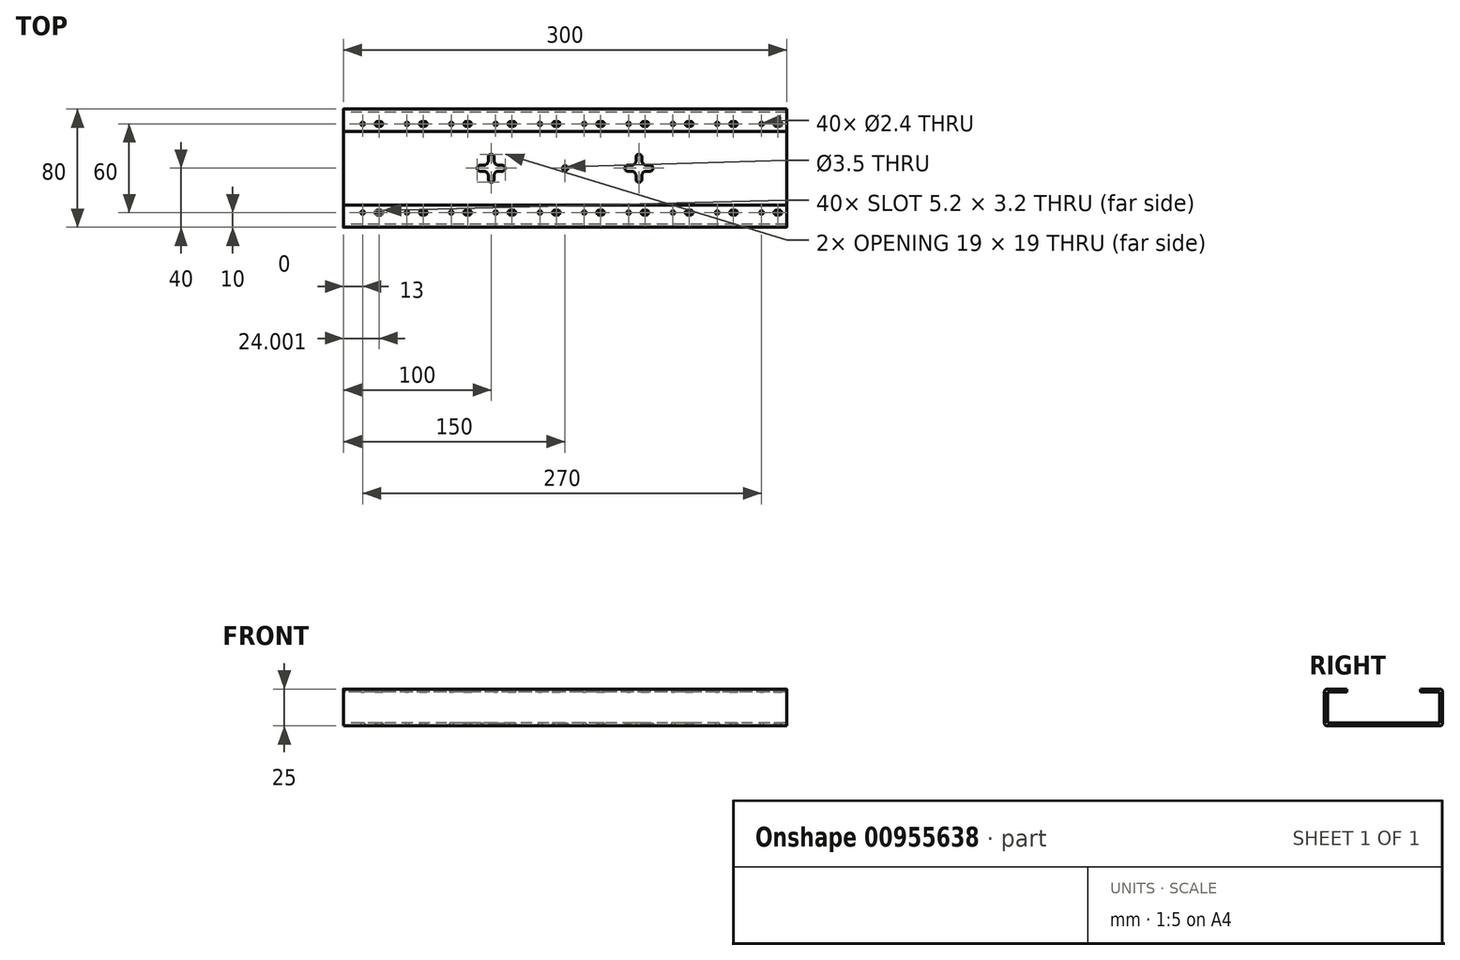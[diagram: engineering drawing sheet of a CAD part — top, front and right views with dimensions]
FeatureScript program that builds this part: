
annotation { "Feature Type Name" : "Feature", "Feature Type Description" : "" }
export const myFeature = defineFeature(function(context is Context, id is Id, definition is map)
    precondition{}
    {
        {
            var Q0;
            Q0=qCreatedBy(makeId("Right.planeOp"),FACE);
            var sketch = newSketch(context, id + "F0", { "sketchPlane" : qUnion([Q0])});
            skLineSegment(sketch, "E0", {"start": v(0, 0) * mm, "end": v(40, 0) * mm});
            skLineSegment(sketch, "E1", {"start": v(40, 0) * mm, "end": v(40, 25) * mm});
            skLineSegment(sketch, "E2", {"start": v(40, 25) * mm, "end": v(25, 25) * mm});
            skLineSegment(sketch, "E3", {"start": v(0, 0) * mm, "end": v(-40, 0) * mm});
            skLineSegment(sketch, "E4", {"start": v(-40, 0) * mm, "end": v(-40, 25) * mm});
            skLineSegment(sketch, "E5", {"start": v(-40, 25) * mm, "end": v(-25, 25) * mm});
            skLineSegment(sketch, "E6.0", {"start": v(38, 23) * mm, "end": v(25, 23) * mm});
            skLineSegment(sketch, "E6.1", {"start": v(38, 2) * mm, "end": v(38, 23) * mm});
            skLineSegment(sketch, "E6.2", {"start": v(-38, 23) * mm, "end": v(-25, 23) * mm});
            skLineSegment(sketch, "E6.3", {"start": v(-38, 2) * mm, "end": v(-38, 23) * mm});
            skLineSegment(sketch, "E6.4", {"start": v(0, 2) * mm, "end": v(-38, 2) * mm});
            skLineSegment(sketch, "E6.5", {"start": v(0, 2) * mm, "end": v(38, 2) * mm});
            skLineSegment(sketch, "E7", {"start": v(25, 25) * mm, "end": v(25, 23) * mm});
            skLineSegment(sketch, "E8", {"start": v(-25, 23) * mm, "end": v(-25, 25) * mm});
            skSolve(sketch);
        }
        {
            var Q0;
            Q0 = qSketchRegion(id + "F0", true);
            var Q1;
            Q1=sQuery(id+"F0.wireOp",EDGE,"E0");
            var Q2;
            Q2=sQuery(id+"F0.wireOp",EDGE,"E1");
            var Q3;
            Q3=sQuery(id+"F0.wireOp",EDGE,"E2");
            var Q4;
            Q4=sQuery(id+"F0.wireOp",EDGE,"E3");
            var Q5;
            Q5=sQuery(id+"F0.wireOp",EDGE,"E4");
            var Q6;
            Q6=sQuery(id+"F0.wireOp",EDGE,"E5");
            var Q7;
            Q7=sQuery(id+"F0.wireOp",EDGE,"E6.0");
            var Q8;
            Q8=sQuery(id+"F0.wireOp",EDGE,"E7");
            var Q9;
            Q9=sQuery(id+"F0.wireOp",EDGE,"E6.1");
            var Q10;
            Q10=sQuery(id+"F0.wireOp",EDGE,"E6.5");
            var Q11;
            Q11=sQuery(id+"F0.wireOp",EDGE,"E6.4");
            var Q12;
            Q12=sQuery(id+"F0.wireOp",EDGE,"E6.3");
            var Q13;
            Q13=sQuery(id+"F0.wireOp",EDGE,"E6.2");
            var Q14;
            Q14=sQuery(id+"F0.wireOp",EDGE,"E8");
            extrude(context, id + "F1", {"entities" : qUnion([Q0]), "surfaceEntities" : qUnion([Q1, Q2, Q3, Q4, Q5, Q6, Q7, Q8, Q9, Q10, Q11, Q12, Q13, Q14]), "endBound" : BoundingType.SYMMETRIC, "depth" : 300 * mm, "offsetDistance" : 25 * mm});
        }
        {
            var Q0;
            Q0=makeQuery(id+"F1.opExtrude","SWEPT_FACE",FACE,{"disambiguationData":[OSD([sQuery(id+"F0.wireOp",EDGE,"E0"),sQuery(id+"F0.wireOp",EDGE,"E3")])]});
            var sketch = newSketch(context, id + "F2", { "sketchPlane" : qUnion([Q0])});
            skCircle(sketch, "E9", {"center": v(133, 30) * mm, "radius": 1.2 * mm});
            skLineSegment(sketch, "E10", {"start": v(142.9, 31.6) * mm, "end": v(145, 31.6) * mm});
            skLineSegment(sketch, "E11", {"start": v(142.97, 28.4) * mm, "end": v(145.03, 28.4) * mm});
            skArc(sketch, "E12", {"start": v(142.9, 31.6) * mm, "mid": v(141.4, 29.93) * mm, "end": v(143.03, 28.4) * mm});
            skArc(sketch, "E13", {"start": v(145.03, 28.4) * mm, "mid": v(146.6, 30.02) * mm, "end": v(145, 31.6) * mm});
            skLineSegment(sketch, "E14.1.0.0", {"start": v(112.97, 28.4) * mm, "end": v(115.03, 28.4) * mm});
            skCircle(sketch, "E14.1.0.1", {"center": v(103, 30) * mm, "radius": 1.2 * mm});
            skArc(sketch, "E14.1.0.2", {"start": v(112.9, 31.6) * mm, "mid": v(111.4, 29.93) * mm, "end": v(113.03, 28.4) * mm});
            skArc(sketch, "E14.1.0.3", {"start": v(115.03, 28.4) * mm, "mid": v(116.6, 30.02) * mm, "end": v(115, 31.6) * mm});
            skLineSegment(sketch, "E14.1.0.4", {"start": v(112.9, 31.6) * mm, "end": v(115, 31.6) * mm});
            skLineSegment(sketch, "E14.2.0.0", {"start": v(82.97, 28.4) * mm, "end": v(85.03, 28.4) * mm});
            skCircle(sketch, "E14.2.0.1", {"center": v(73, 30) * mm, "radius": 1.2 * mm});
            skArc(sketch, "E14.2.0.2", {"start": v(82.9, 31.6) * mm, "mid": v(81.4, 29.93) * mm, "end": v(83.03, 28.4) * mm});
            skArc(sketch, "E14.2.0.3", {"start": v(85.03, 28.4) * mm, "mid": v(86.6, 30.02) * mm, "end": v(85, 31.6) * mm});
            skLineSegment(sketch, "E14.2.0.4", {"start": v(82.9, 31.6) * mm, "end": v(85, 31.6) * mm});
            skLineSegment(sketch, "E14.direction1", {"start": v(133, 30) * mm, "end": v(103, 30) * mm, "construction": true});
            skLineSegment(sketch, "E15.0.3.0", {"start": v(52.97, 28.4) * mm, "end": v(55.03, 28.4) * mm});
            skCircle(sketch, "E15.3.3.0", {"center": v(43, 30) * mm, "radius": 1.2 * mm});
            skArc(sketch, "E15.5.3.0", {"start": v(52.9, 31.6) * mm, "mid": v(51.4, 29.93) * mm, "end": v(53.03, 28.4) * mm});
            skArc(sketch, "E15.9.3.0", {"start": v(55.03, 28.4) * mm, "mid": v(56.6, 30.02) * mm, "end": v(55, 31.6) * mm});
            skLineSegment(sketch, "E15.13.3.0", {"start": v(52.9, 31.6) * mm, "end": v(55, 31.6) * mm});
            skLineSegment(sketch, "E15.0.4.0", {"start": v(22.97, 28.4) * mm, "end": v(25.03, 28.4) * mm});
            skCircle(sketch, "E15.3.4.0", {"center": v(13, 30) * mm, "radius": 1.2 * mm});
            skArc(sketch, "E15.5.4.0", {"start": v(22.9, 31.6) * mm, "mid": v(21.4, 29.93) * mm, "end": v(23.03, 28.4) * mm});
            skArc(sketch, "E15.9.4.0", {"start": v(25.03, 28.4) * mm, "mid": v(26.6, 30.02) * mm, "end": v(25, 31.6) * mm});
            skLineSegment(sketch, "E15.13.4.0", {"start": v(22.9, 31.6) * mm, "end": v(25, 31.6) * mm});
            skLineSegment(sketch, "E15.0.5.0", {"start": v(-7.03, 28.4) * mm, "end": v(-4.97, 28.4) * mm});
            skCircle(sketch, "E15.3.5.0", {"center": v(-17, 30) * mm, "radius": 1.2 * mm});
            skArc(sketch, "E15.5.5.0", {"start": v(-7.1, 31.6) * mm, "mid": v(-8.6, 29.93) * mm, "end": v(-6.97, 28.4) * mm});
            skArc(sketch, "E15.9.5.0", {"start": v(-4.97, 28.4) * mm, "mid": v(-3.4, 30.02) * mm, "end": v(-5, 31.6) * mm});
            skLineSegment(sketch, "E15.13.5.0", {"start": v(-7.1, 31.6) * mm, "end": v(-5, 31.6) * mm});
            skLineSegment(sketch, "E15.0.6.0", {"start": v(-37.03, 28.4) * mm, "end": v(-34.97, 28.4) * mm});
            skCircle(sketch, "E15.3.6.0", {"center": v(-47, 30) * mm, "radius": 1.2 * mm});
            skArc(sketch, "E15.5.6.0", {"start": v(-37.1, 31.6) * mm, "mid": v(-38.6, 29.93) * mm, "end": v(-36.97, 28.4) * mm});
            skArc(sketch, "E15.9.6.0", {"start": v(-34.97, 28.4) * mm, "mid": v(-33.4, 30.02) * mm, "end": v(-35, 31.6) * mm});
            skLineSegment(sketch, "E15.13.6.0", {"start": v(-37.1, 31.6) * mm, "end": v(-35, 31.6) * mm});
            skLineSegment(sketch, "E15.0.7.0", {"start": v(-67.03, 28.4) * mm, "end": v(-64.97, 28.4) * mm});
            skCircle(sketch, "E15.3.7.0", {"center": v(-77, 30) * mm, "radius": 1.2 * mm});
            skArc(sketch, "E15.5.7.0", {"start": v(-67.1, 31.6) * mm, "mid": v(-68.6, 29.93) * mm, "end": v(-66.97, 28.4) * mm});
            skArc(sketch, "E15.9.7.0", {"start": v(-64.97, 28.4) * mm, "mid": v(-63.4, 30.02) * mm, "end": v(-65, 31.6) * mm});
            skLineSegment(sketch, "E15.13.7.0", {"start": v(-67.1, 31.6) * mm, "end": v(-65, 31.6) * mm});
            skLineSegment(sketch, "E15.0.8.0", {"start": v(-97.03, 28.4) * mm, "end": v(-94.97, 28.4) * mm});
            skCircle(sketch, "E15.3.8.0", {"center": v(-107, 30) * mm, "radius": 1.2 * mm});
            skArc(sketch, "E15.5.8.0", {"start": v(-97.1, 31.6) * mm, "mid": v(-98.6, 29.93) * mm, "end": v(-96.97, 28.4) * mm});
            skArc(sketch, "E15.9.8.0", {"start": v(-94.97, 28.4) * mm, "mid": v(-93.4, 30.02) * mm, "end": v(-95, 31.6) * mm});
            skLineSegment(sketch, "E15.13.8.0", {"start": v(-97.1, 31.6) * mm, "end": v(-95, 31.6) * mm});
            skLineSegment(sketch, "E15.0.9.0", {"start": v(-127.03, 28.4) * mm, "end": v(-124.97, 28.4) * mm});
            skCircle(sketch, "E15.3.9.0", {"center": v(-137, 30) * mm, "radius": 1.2 * mm});
            skArc(sketch, "E15.5.9.0", {"start": v(-127.1, 31.6) * mm, "mid": v(-128.6, 29.93) * mm, "end": v(-126.97, 28.4) * mm});
            skArc(sketch, "E15.9.9.0", {"start": v(-124.97, 28.4) * mm, "mid": v(-123.4, 30.02) * mm, "end": v(-125, 31.6) * mm});
            skLineSegment(sketch, "E15.13.9.0", {"start": v(-127.1, 31.6) * mm, "end": v(-125, 31.6) * mm});
            skLineSegment(sketch, "E16.MirrorCS", {"start": v(-127.1, -31.6) * mm, "end": v(-125, -31.6) * mm});
            skLineSegment(sketch, "E17.MirrorCS", {"start": v(-127.03, -28.4) * mm, "end": v(-124.97, -28.4) * mm});
            skArc(sketch, "E18.MirrorCS", {"start": v(-127.1, -31.6) * mm, "mid": v(-128.6, -29.93) * mm, "end": v(-126.97, -28.4) * mm});
            skArc(sketch, "E19.MirrorCS", {"start": v(-124.97, -28.4) * mm, "mid": v(-123.4, -30.02) * mm, "end": v(-125, -31.6) * mm});
            skCircle(sketch, "E20.MirrorC", {"center": v(-137, -30) * mm, "radius": 1.2 * mm});
            skLineSegment(sketch, "E21.MirrorCS", {"start": v(-97.03, -28.4) * mm, "end": v(-94.97, -28.4) * mm});
            skLineSegment(sketch, "E22.MirrorCS", {"start": v(-97.1, -31.6) * mm, "end": v(-95, -31.6) * mm});
            skArc(sketch, "E23.MirrorCS", {"start": v(-94.97, -28.4) * mm, "mid": v(-93.4, -30.02) * mm, "end": v(-95, -31.6) * mm});
            skArc(sketch, "E24.MirrorCS", {"start": v(-97.1, -31.6) * mm, "mid": v(-98.6, -29.93) * mm, "end": v(-96.97, -28.4) * mm});
            skCircle(sketch, "E25.MirrorC", {"center": v(-107, -30) * mm, "radius": 1.2 * mm});
            skLineSegment(sketch, "E26.MirrorCS", {"start": v(-67.1, -31.6) * mm, "end": v(-65, -31.6) * mm});
            skLineSegment(sketch, "E27.MirrorCS", {"start": v(-67.03, -28.4) * mm, "end": v(-64.97, -28.4) * mm});
            skArc(sketch, "E28.MirrorCS", {"start": v(-67.1, -31.6) * mm, "mid": v(-68.6, -29.93) * mm, "end": v(-66.97, -28.4) * mm});
            skArc(sketch, "E29.MirrorCS", {"start": v(-64.97, -28.4) * mm, "mid": v(-63.4, -30.02) * mm, "end": v(-65, -31.6) * mm});
            skCircle(sketch, "E30.MirrorC", {"center": v(-77, -30) * mm, "radius": 1.2 * mm});
            skLineSegment(sketch, "E31.MirrorCS", {"start": v(-37.1, -31.6) * mm, "end": v(-35, -31.6) * mm});
            skArc(sketch, "E32.MirrorCS", {"start": v(-37.1, -31.6) * mm, "mid": v(-38.6, -29.93) * mm, "end": v(-36.97, -28.4) * mm});
            skArc(sketch, "E33.MirrorCS", {"start": v(-34.97, -28.4) * mm, "mid": v(-33.4, -30.02) * mm, "end": v(-35, -31.6) * mm});
            skLineSegment(sketch, "E34.MirrorCS", {"start": v(-37.03, -28.4) * mm, "end": v(-34.97, -28.4) * mm});
            skCircle(sketch, "E35.MirrorC", {"center": v(-47, -30) * mm, "radius": 1.2 * mm});
            skLineSegment(sketch, "E36.MirrorCS", {"start": v(-7.03, -28.4) * mm, "end": v(-4.97, -28.4) * mm});
            skArc(sketch, "E37.MirrorCS", {"start": v(-7.1, -31.6) * mm, "mid": v(-8.6, -29.93) * mm, "end": v(-6.97, -28.4) * mm});
            skArc(sketch, "E38.MirrorCS", {"start": v(-4.97, -28.4) * mm, "mid": v(-3.4, -30.02) * mm, "end": v(-5, -31.6) * mm});
            skLineSegment(sketch, "E39.MirrorCS", {"start": v(-7.1, -31.6) * mm, "end": v(-5, -31.6) * mm});
            skCircle(sketch, "E40.MirrorC", {"center": v(-17, -30) * mm, "radius": 1.2 * mm});
            skLineSegment(sketch, "E41.MirrorCS", {"start": v(22.9, -31.6) * mm, "end": v(25, -31.6) * mm});
            skArc(sketch, "E42.MirrorCS", {"start": v(25.03, -28.4) * mm, "mid": v(26.6, -30.02) * mm, "end": v(25, -31.6) * mm});
            skLineSegment(sketch, "E43.MirrorCS", {"start": v(22.97, -28.4) * mm, "end": v(25.03, -28.4) * mm});
            skArc(sketch, "E44.MirrorCS", {"start": v(22.9, -31.6) * mm, "mid": v(21.4, -29.93) * mm, "end": v(23.03, -28.4) * mm});
            skCircle(sketch, "E45.MirrorC", {"center": v(13, -30) * mm, "radius": 1.2 * mm});
            skLineSegment(sketch, "E46.MirrorCS", {"start": v(52.9, -31.6) * mm, "end": v(55, -31.6) * mm});
            skArc(sketch, "E47.MirrorCS", {"start": v(52.9, -31.6) * mm, "mid": v(51.4, -29.93) * mm, "end": v(53.03, -28.4) * mm});
            skArc(sketch, "E48.MirrorCS", {"start": v(55.03, -28.4) * mm, "mid": v(56.6, -30.02) * mm, "end": v(55, -31.6) * mm});
            skLineSegment(sketch, "E49.MirrorCS", {"start": v(52.97, -28.4) * mm, "end": v(55.03, -28.4) * mm});
            skCircle(sketch, "E50.MirrorC", {"center": v(43, -30) * mm, "radius": 1.2 * mm});
            skCircle(sketch, "E51.MirrorC", {"center": v(73, -30) * mm, "radius": 1.2 * mm});
            skLineSegment(sketch, "E52.MirrorCS", {"start": v(82.97, -28.4) * mm, "end": v(85.03, -28.4) * mm});
            skArc(sketch, "E53.MirrorCS", {"start": v(85.03, -28.4) * mm, "mid": v(86.6, -30.02) * mm, "end": v(85, -31.6) * mm});
            skLineSegment(sketch, "E54.MirrorCS", {"start": v(82.9, -31.6) * mm, "end": v(85, -31.6) * mm});
            skArc(sketch, "E55.MirrorCS", {"start": v(82.9, -31.6) * mm, "mid": v(81.4, -29.93) * mm, "end": v(83.03, -28.4) * mm});
            skLineSegment(sketch, "E56.MirrorCS", {"start": v(112.9, -31.6) * mm, "end": v(115, -31.6) * mm});
            skLineSegment(sketch, "E57.MirrorCS", {"start": v(142.9, -31.6) * mm, "end": v(145, -31.6) * mm});
            skArc(sketch, "E58.MirrorCS", {"start": v(142.9, -31.6) * mm, "mid": v(141.4, -29.93) * mm, "end": v(143.03, -28.4) * mm});
            skLineSegment(sketch, "E59.MirrorCS", {"start": v(112.97, -28.4) * mm, "end": v(115.03, -28.4) * mm});
            skLineSegment(sketch, "E60.MirrorCS", {"start": v(142.97, -28.4) * mm, "end": v(145.03, -28.4) * mm});
            skCircle(sketch, "E61.MirrorC", {"center": v(133, -30) * mm, "radius": 1.2 * mm});
            skArc(sketch, "E62.MirrorCS", {"start": v(145.03, -28.4) * mm, "mid": v(146.6, -30.02) * mm, "end": v(145, -31.6) * mm});
            skArc(sketch, "E63.MirrorCS", {"start": v(112.9, -31.6) * mm, "mid": v(111.4, -29.93) * mm, "end": v(113.03, -28.4) * mm});
            skArc(sketch, "E64.MirrorCS", {"start": v(115.03, -28.4) * mm, "mid": v(116.6, -30.02) * mm, "end": v(115, -31.6) * mm});
            skCircle(sketch, "E65.MirrorC", {"center": v(103, -30) * mm, "radius": 1.2 * mm});
            skLineSegment(sketch, "E66.MirrorCS", {"start": v(133, -30) * mm, "end": v(103, -30) * mm, "construction": true});
            skSolve(sketch);
        }
        {
            var Q0;
            Q0 = qSketchRegion(id + "F2", true);
            extrude(context, id + "F3", {"entities" : qUnion([Q0]), "operationType" : NewBodyOperationType.REMOVE, "endBound" : BoundingType.THROUGH_ALL, "oppositeDirection" : true, "depth" : 25 * mm, "offsetDistance" : 25 * mm});
        }
        {
            var Q0;
            Q0=makeQuery(id+"F1.opExtrude","SWEPT_EDGE",EDGE,{"disambiguationData":[OSD([sQuery(id+"F0.wireOp",EDGE,"E1"),sQuery(id+"F0.wireOp",EDGE,"E2")])]});
            var Q1;
            Q1=makeQuery(id+"F1.opExtrude","SWEPT_EDGE",EDGE,{"disambiguationData":[OSD([sQuery(id+"F0.wireOp",EDGE,"E0"),sQuery(id+"F0.wireOp",EDGE,"E1")])]});
            var Q2;
            Q2=makeQuery(id+"F1.opExtrude","SWEPT_EDGE",EDGE,{"disambiguationData":[OSD([sQuery(id+"F0.wireOp",EDGE,"E3"),sQuery(id+"F0.wireOp",EDGE,"E4")])]});
            var Q3;
            Q3=makeQuery(id+"F1.opExtrude","SWEPT_EDGE",EDGE,{"disambiguationData":[OSD([sQuery(id+"F0.wireOp",EDGE,"E4"),sQuery(id+"F0.wireOp",EDGE,"E5")])]});
            fillet(context, id + "F4", {"entities" : qUnion([Q0, Q1, Q2, Q3]), "radius" : 2 * mm, "tangentPropagation" : true, "allowEdgeOverflow" : false});
        }
        {
            var Q0;
            Q0=makeQuery(id+"F1.opExtrude","CAP_EDGE",EDGE,{"disambiguationData":[OSD([sQuery(id+"F0.wireOp",EDGE,"E7")])],"isStart":true});
            var Q1;
            Q1=makeQuery(id+"F1.opExtrude","CAP_EDGE",EDGE,{"disambiguationData":[OSD([sQuery(id+"F0.wireOp",EDGE,"E8")])],"isStart":true});
            var Q2;
            Q2=makeQuery(id+"F1.opExtrude","CAP_EDGE",EDGE,{"disambiguationData":[OSD([sQuery(id+"F0.wireOp",EDGE,"E7")])],"isStart":false});
            var Q3;
            Q3=makeQuery(id+"F1.opExtrude","CAP_EDGE",EDGE,{"disambiguationData":[OSD([sQuery(id+"F0.wireOp",EDGE,"E8")])],"isStart":false});
            fillet(context, id + "F5", {"entities" : qUnion([Q0, Q1, Q2, Q3]), "radius" : 1.5 * mm, "tangentPropagation" : true, "allowEdgeOverflow" : false});
        }
        {
            var Q0;
            Q0=makeQuery(id+"F1.opExtrude","SWEPT_FACE",FACE,{"disambiguationData":[OSD([sQuery(id+"F0.wireOp",EDGE,"E0"),sQuery(id+"F0.wireOp",EDGE,"E3")])]});
            var sketch = newSketch(context, id + "F6", { "sketchPlane" : qUnion([Q0])});
            skCircle(sketch, "E67", {"center": v(0, 0) * mm, "radius": 1.75 * mm});
            skLineSegment(sketch, "E68", {"start": v(-57.5, 0) * mm, "end": v(-42.5, 0) * mm});
            skLineSegment(sketch, "E69", {"start": v(-50, 7.5) * mm, "end": v(-50, -7.5) * mm});
            skArc(sketch, "E70.0.startCap", {"start": v(-57.5, -2) * mm, "mid": v(-59.5, 0) * mm, "end": v(-57.5, 2) * mm});
            skArc(sketch, "E70.0.endCap", {"start": v(-42.5, 2) * mm, "mid": v(-40.5, 0) * mm, "end": v(-42.5, -2) * mm});
            skLineSegment(sketch, "E70.0.left", {"start": v(-57.5, 2) * mm, "end": v(-42.5, 2) * mm});
            skLineSegment(sketch, "E70.0.right", {"start": v(-57.5, -2) * mm, "end": v(-42.5, -2) * mm});
            skArc(sketch, "E70.1.startCap", {"start": v(-52, 7.5) * mm, "mid": v(-50, 9.5) * mm, "end": v(-48, 7.5) * mm});
            skArc(sketch, "E70.1.endCap", {"start": v(-48, -7.5) * mm, "mid": v(-50, -9.5) * mm, "end": v(-52, -7.5) * mm});
            skLineSegment(sketch, "E70.1.left", {"start": v(-48, 7.5) * mm, "end": v(-48, -7.5) * mm});
            skLineSegment(sketch, "E70.1.right", {"start": v(-52, 7.5) * mm, "end": v(-52, -7.5) * mm});
            skLineSegment(sketch, "E71.1.0.0", {"start": v(52, 7.5) * mm, "end": v(52, -7.5) * mm});
            skLineSegment(sketch, "E71.1.0.1", {"start": v(48, 7.5) * mm, "end": v(48, -7.5) * mm});
            skLineSegment(sketch, "E71.1.0.2", {"start": v(42.5, -2) * mm, "end": v(57.5, -2) * mm});
            skLineSegment(sketch, "E71.1.0.3", {"start": v(50, 7.5) * mm, "end": v(50, -7.5) * mm});
            skLineSegment(sketch, "E71.1.0.4", {"start": v(42.5, 0) * mm, "end": v(57.5, 0) * mm});
            skLineSegment(sketch, "E71.1.0.5", {"start": v(42.5, 2) * mm, "end": v(57.5, 2) * mm});
            skArc(sketch, "E71.1.0.6", {"start": v(42.5, -2) * mm, "mid": v(40.5, 0) * mm, "end": v(42.5, 2) * mm});
            skArc(sketch, "E71.1.0.7", {"start": v(57.5, 2) * mm, "mid": v(59.5, 0) * mm, "end": v(57.5, -2) * mm});
            skArc(sketch, "E71.1.0.8", {"start": v(52, -7.5) * mm, "mid": v(50, -9.5) * mm, "end": v(48, -7.5) * mm});
            skArc(sketch, "E71.1.0.9", {"start": v(48, 7.5) * mm, "mid": v(50, 9.5) * mm, "end": v(52, 7.5) * mm});
            skLineSegment(sketch, "E71.direction1", {"start": v(-52, -7.5) * mm, "end": v(48, -7.5) * mm, "construction": true});
            skSolve(sketch);
        }
        {
            var Q0;
            Q0 = qSketchRegion(id + "F6", true);
            extrude(context, id + "F7", {"entities" : qUnion([Q0]), "operationType" : NewBodyOperationType.REMOVE, "oppositeDirection" : true, "depth" : 2 * mm, "offsetDistance" : 25 * mm});
        }
        {
            var Q0;
            Q0=makeQuery(id+"F7.boolean.opBoolean","COPY",EDGE,{"derivedFrom":makeQuery(id+"F7.opExtrude","SWEPT_EDGE",EDGE,{"disambiguationData":[OSD([sQuery(id+"F6.wireOp",EDGE,"E70.0.right"),sQuery(id+"F6.wireOp",EDGE,"E70.1.right")])]})});
            var Q1;
            Q1=makeQuery(id+"F7.boolean.opBoolean","COPY",EDGE,{"derivedFrom":makeQuery(id+"F7.opExtrude","SWEPT_EDGE",EDGE,{"disambiguationData":[OSD([sQuery(id+"F6.wireOp",EDGE,"E70.0.right"),sQuery(id+"F6.wireOp",EDGE,"E70.1.left")])]})});
            var Q2;
            Q2=makeQuery(id+"F7.boolean.opBoolean","COPY",EDGE,{"derivedFrom":makeQuery(id+"F7.opExtrude","SWEPT_EDGE",EDGE,{"disambiguationData":[OSD([sQuery(id+"F6.wireOp",EDGE,"E70.0.left"),sQuery(id+"F6.wireOp",EDGE,"E70.1.left")])]})});
            var Q3;
            Q3=makeQuery(id+"F7.boolean.opBoolean","COPY",EDGE,{"derivedFrom":makeQuery(id+"F7.opExtrude","SWEPT_EDGE",EDGE,{"disambiguationData":[OSD([sQuery(id+"F6.wireOp",EDGE,"E70.0.left"),sQuery(id+"F6.wireOp",EDGE,"E70.1.right")])]})});
            var Q4;
            Q4=makeQuery(id+"F7.boolean.opBoolean","COPY",EDGE,{"derivedFrom":makeQuery(id+"F7.opExtrude","SWEPT_EDGE",EDGE,{"disambiguationData":[OSD([sQuery(id+"F6.wireOp",EDGE,"E71.1.0.1"),sQuery(id+"F6.wireOp",EDGE,"E71.1.0.5")])]})});
            var Q5;
            Q5=makeQuery(id+"F7.boolean.opBoolean","COPY",EDGE,{"derivedFrom":makeQuery(id+"F7.opExtrude","SWEPT_EDGE",EDGE,{"disambiguationData":[OSD([sQuery(id+"F6.wireOp",EDGE,"E71.1.0.0"),sQuery(id+"F6.wireOp",EDGE,"E71.1.0.5")])]})});
            var Q6;
            Q6=makeQuery(id+"F7.boolean.opBoolean","COPY",EDGE,{"derivedFrom":makeQuery(id+"F7.opExtrude","SWEPT_EDGE",EDGE,{"disambiguationData":[OSD([sQuery(id+"F6.wireOp",EDGE,"E71.1.0.1"),sQuery(id+"F6.wireOp",EDGE,"E71.1.0.2")])]})});
            var Q7;
            Q7=makeQuery(id+"F7.boolean.opBoolean","COPY",EDGE,{"derivedFrom":makeQuery(id+"F7.opExtrude","SWEPT_EDGE",EDGE,{"disambiguationData":[OSD([sQuery(id+"F6.wireOp",EDGE,"E71.1.0.0"),sQuery(id+"F6.wireOp",EDGE,"E71.1.0.2")])]})});
            fillet(context, id + "F8", {"entities" : qUnion([Q0, Q1, Q2, Q3, Q4, Q5, Q6, Q7]), "radius" : 3 * mm, "tangentPropagation" : true, "allowEdgeOverflow" : false});
        }
    });
